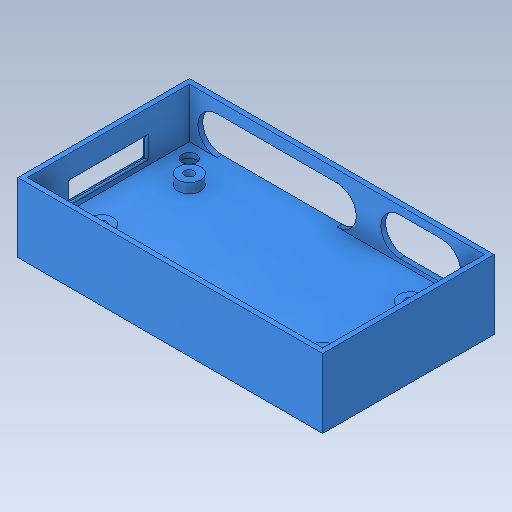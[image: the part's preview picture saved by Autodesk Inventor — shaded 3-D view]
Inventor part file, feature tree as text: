
AUTODESK INVENTOR PART (.ipt)
format: ipt  version: 2021 (Build 250183000, 183)  size: 267,264 bytes
history: native  units: in
note: dims shown in document units (in); Inventor stores cm internally (conversion verified against a paired STEP export)
features: sketch x7, extrude x5, hole x4
ambient origin geometry x8: Origin, YZ Plane, XZ Plane, XY Plane, X Axis, Y Axis, Z Axis, Center Point
bodies: Solid1 (feature_tree)
feature tree (16):
  extrude  "Extrusion1"  Depth=1.7717in
  extrude  "Extrusion2"  Depth=0.05in
  extrude  "Extrusion3"  Depth=0.515in
  extrude  "ExtrusionForRibbonCableHole"  Depth=0.9055in
  extrude  "ExtrusionForSideHoles"  Depth=0.7874in
  hole  "Hole9"  [1 undecoded]
  hole  "Hole13"  [1 undecoded]
  hole  "Hole16"  [1 undecoded]
  sketch  "Sketch1"  dims[d0=3.1496in d1=1.7717in]
  sketch  "Sketch2"  dims[d2=0.2in d3=0.0in d4=0.05in]
  sketch  "Sketch3"  dims[d5=0.05in d6=0.515in]
  sketch  "Sketch5"  dims[d7=0.0in d8=0.9055in]
  sketch  "Sketch22"  dims[d9=2.2835in d17=0.7874in d19=2.2835in]
  hole  "Hole12"  [1 undecoded]
  sketch  "Sketch23"  dims[d20=0.7874in d22=0.9055in d25=0.2362in]
  sketch  "Sketch25"  dims[d26=0.1in d27=0.0in d35=0.7874in d36=0.1969in d37=1.0in d38=0.0in d39=0.3937in d40=1.0433in d41=1.1024in d42=1.9252in d43=0.3937in d44=0.7087in d45=0.3937in d46=0.7874in d47=2.4213in d50=0.2362in d51=0.1969in d52=0.1969in d97=0.05in d98=0.0in d99=0.35in d100=0.0167in d138=0.1495in d139=0.75in d140=0.375in d141=0.25in d142=0.5635in d143=1.0in d144=0.0in d145=0.191in d146=0.75in d147=0.375in d148=0.25in d149=0.5635in d150=0.15in d151=0.0in d166=0.096in d167=0.75in d168=0.1285in d169=0.157in d170=0.5635in d171=1.0in d172=0.8108in]
note: 4 required parameter values undecoded (feature->parameter linkage not recoverable at this tier; creation-order binding heuristic only, values carry confidence <= 0.55)
